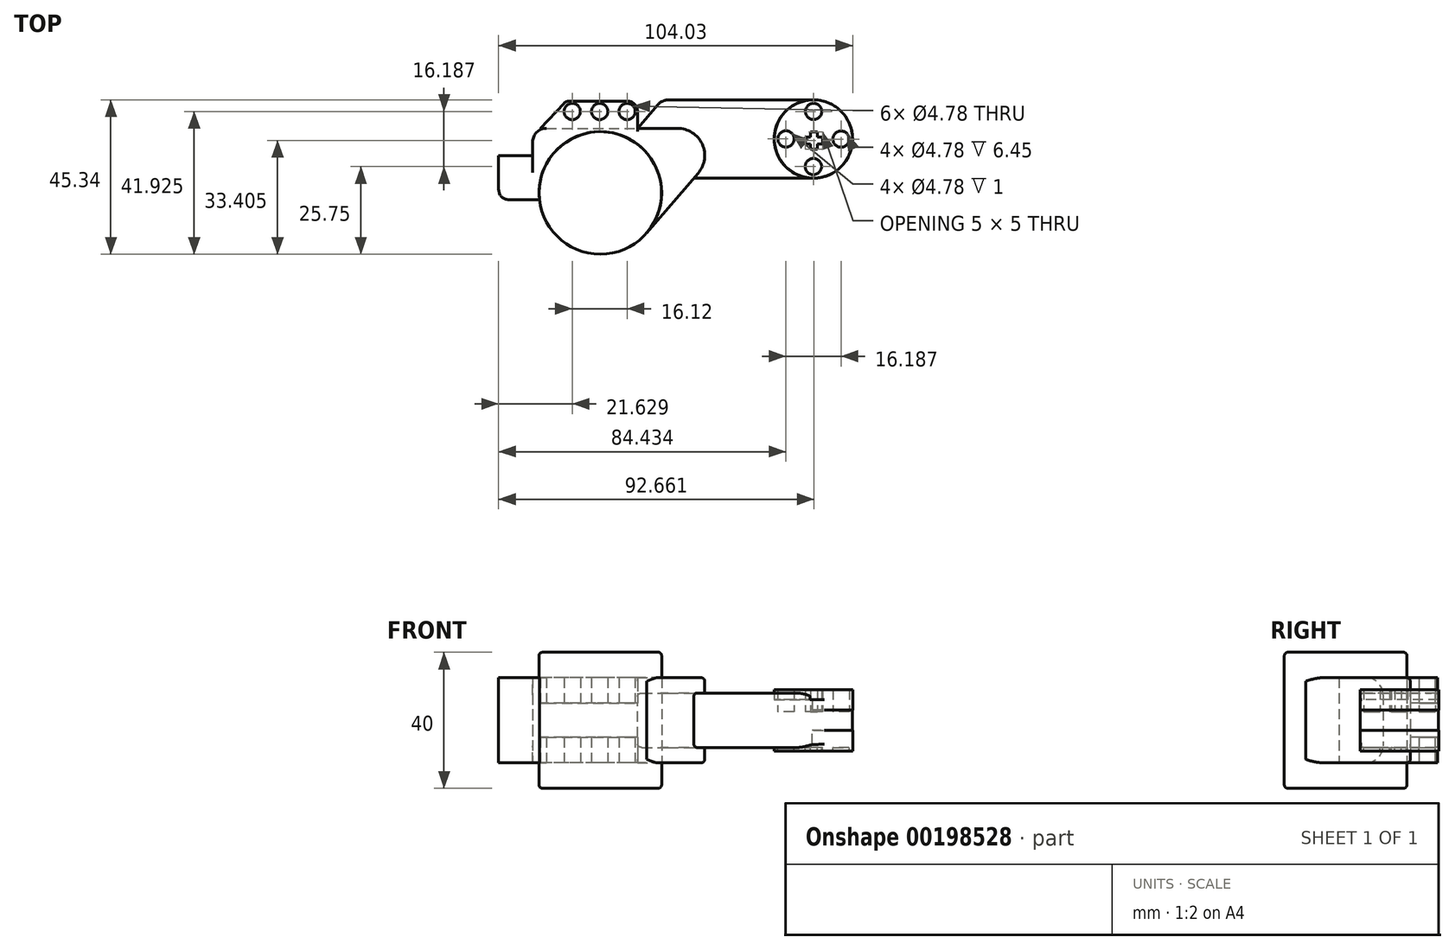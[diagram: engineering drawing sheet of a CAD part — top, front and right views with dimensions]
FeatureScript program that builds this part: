
annotation { "Feature Type Name" : "Feature", "Feature Type Description" : "" }
export const myFeature = defineFeature(function(context is Context, id is Id, definition is map)
    precondition{}
    {
        {
            var Q0;
            Q0=qCreatedBy(makeId("Top.planeOp"),FACE);
            var sketch = newSketch(context, id + "F0", { "sketchPlane" : qUnion([Q0])});
            skCircle(sketch, "E0", {"center": v(-41.3, 0) * mm, "radius": 18 * mm});
            skLineSegment(sketch, "E1", {"start": v(-57.19, 19) * mm, "end": v(-18.63, 19) * mm});
            skLineSegment(sketch, "E2", {"start": v(-12.57, 5.78) * mm, "end": v(-27.66, -11.74) * mm});
            skLineSegment(sketch, "E3", {"start": v(-61.19, 15) * mm, "end": v(-61.19, 11) * mm});
            skLineSegment(sketch, "E4", {"start": v(-61.19, 11) * mm, "end": v(-71.19, 11) * mm});
            skLineSegment(sketch, "E5", {"start": v(-71.19, 11) * mm, "end": v(-71.19, 1) * mm});
            skPoint(sketch, "E6.visualSharp", {"position": v(-1.19, 19) * mm});
            skLineSegment(sketch, "E7", {"start": v(-68.19, -2) * mm, "end": v(-59.19, -2) * mm});
            skArc(sketch, "E8.filletArc", {"start": v(-12.57, 5.78) * mm, "mid": v(-11.36, 14.33) * mm, "end": v(-18.63, 19) * mm});
            skPoint(sketch, "E9.visualSharp", {"position": v(-61.19, 19) * mm});
            skArc(sketch, "E9.filletArc", {"start": v(-57.19, 19) * mm, "mid": v(-60.02, 17.83) * mm, "end": v(-61.19, 15) * mm});
            skPoint(sketch, "E10.visualSharp", {"position": v(-71.19, -2) * mm});
            skArc(sketch, "E10.filletArc", {"start": v(-71.19, 1) * mm, "mid": v(-70.3, -1.12) * mm, "end": v(-68.19, -2) * mm});
            skLineSegment(sketch, "E11", {"start": v(-33.44, 27) * mm, "end": v(-50.5, 27) * mm});
            skLineSegment(sketch, "E12", {"start": v(-51.96, 26.37) * mm, "end": v(-60.1, 17.74) * mm});
            skLineSegment(sketch, "E13", {"start": v(-30.37, 23.92) * mm, "end": v(-30.37, 19) * mm});
            skPoint(sketch, "E14.visualSharp", {"position": v(-51.37, 27) * mm});
            skArc(sketch, "E14.filletArc", {"start": v(-50.5, 27) * mm, "mid": v(-51.3, 26.84) * mm, "end": v(-51.96, 26.37) * mm});
            skPoint(sketch, "E15.visualSharp", {"position": v(-30.37, 27) * mm});
            skArc(sketch, "E15.filletArc", {"start": v(-30.37, 23.92) * mm, "mid": v(-31.27, 26.1) * mm, "end": v(-33.44, 27) * mm});
            skLineSegment(sketch, "E16", {"start": v(-30.37, 19) * mm, "end": v(-58.91, 19) * mm, "construction": true});
            skLineSegment(sketch, "E17", {"start": v(-30.37, 19) * mm, "end": v(-23.19, 27.34) * mm});
            skLineSegment(sketch, "E18", {"start": v(-23.19, 27.34) * mm, "end": v(21.31, 27.34) * mm});
            skLineSegment(sketch, "E19", {"start": v(32.81, 15.84) * mm, "end": v(32.81, 15.84) * mm});
            skLineSegment(sketch, "E20", {"start": v(21.31, 4.34) * mm, "end": v(-13.81, 4.34) * mm});
            skPoint(sketch, "E21.visualSharp", {"position": v(32.81, 27.34) * mm});
            skArc(sketch, "E21.filletArc", {"start": v(32.81, 15.84) * mm, "mid": v(29.44, 23.97) * mm, "end": v(21.31, 27.34) * mm});
            skPoint(sketch, "E22.visualSharp", {"position": v(32.81, 4.34) * mm});
            skArc(sketch, "E22.filletArc", {"start": v(21.31, 4.34) * mm, "mid": v(29.44, 7.7) * mm, "end": v(32.81, 15.84) * mm});
            skLineSegment(sketch, "E23", {"start": v(-58.91, 19) * mm, "end": v(-30.37, 19) * mm});
            skCircle(sketch, "E24", {"center": v(-33.44, 23.92) * mm, "radius": 2.4 * mm});
            skCircle(sketch, "E25", {"center": v(-33.44, 23.92) * mm, "radius": 3.08 * mm, "construction": true});
            skCircle(sketch, "E26.1.0.0", {"center": v(-41.5, 23.92) * mm, "radius": 2.4 * mm});
            skCircle(sketch, "E26.2.0.0", {"center": v(-49.56, 23.92) * mm, "radius": 2.4 * mm});
            skLineSegment(sketch, "E26.direction1", {"start": v(-33.44, 23.92) * mm, "end": v(-41.5, 23.92) * mm, "construction": true});
            skSolve(sketch);
        }
        {
            var Q0;
            {var subQ0=sQuery(id+"F0.wireOp",EDGE,"E0");var subQ1=makeQuery(id+"F0.imprint","INTERSECT",VERTEX,{"derivedFrom":[subQ0,sQuery(id+"F0.wireOp",EDGE,"E2")]});Q0=makeQuery(id+"F0.imprint","IMPRINT",FACE,{"disambiguationData":[TD([[makeQuery(id+"F0.imprint","IMPRINT",EDGE,{"disambiguationData":[TD([[subQ1,1.0]])],"derivedFrom":subQ0}),1.0]])]});}
            var Q1;
            Q1=sQuery(id+"F0.wireOp",EDGE,"E0");
            extrude(context, id + "F1", {"entities" : qUnion([Q0]), "surfaceEntities" : qUnion([Q1]), "endBound" : BoundingType.SYMMETRIC, "depth" : 40 * mm});
        }
        {
            var Q0;
            {var subQ0=sQuery(id+"F0.wireOp",EDGE,"E3");Q0=makeQuery(id+"F0.imprint","IMPRINT",FACE,{"disambiguationData":[TD([[makeQuery(id+"F0.imprint","IMPRINT",EDGE,{"derivedFrom":subQ0}),1.0]])]});}
            var Q1;
            Q1=makeQuery(id+"F0.imprint","IMPRINT",FACE,{"disambiguationData":[TD([[makeQuery(id+"F0.imprint","IMPRINT",EDGE,{"derivedFrom":sQuery(id+"F0.wireOp",EDGE,"E11")}),1.0]])]});
            extrude(context, id + "F2", {"entities" : qUnion([Q0, Q1]), "endBound" : BoundingType.SYMMETRIC, "depth" : 25 * mm});
        }
        {
            var Q0;
            {var subQ0=sQuery(id+"F0.wireOp",EDGE,"E8.filletArc");Q0=makeQuery(id+"F0.imprint","IMPRINT",FACE,{"disambiguationData":[TD([[makeQuery(id+"F0.imprint","IMPRINT",EDGE,{"derivedFrom":subQ0}),-1.0]])]});}
            extrude(context, id + "F3", {"entities" : qUnion([Q0]), "operationType" : NewBodyOperationType.ADD, "endBound" : BoundingType.SYMMETRIC, "depth" : 16 * mm});
        }
        {
            var Q0;
            Q0=makeQuery(id+"F3.opExtrude","SWEPT_EDGE",EDGE,{"disambiguationData":[OSD([sQuery(id+"F0.wireOp",EDGE,"E17"),sQuery(id+"F0.wireOp",EDGE,"E18")])]});
            fillet(context, id + "F4", {"entities" : qUnion([Q0]), "radius" : 4 * mm, "tangentPropagation" : true, "allowEdgeOverflow" : false});
        }
        {
            var Q0;
            Q0=makeQuery(id+"F1.opExtrude","CAP_EDGE",EDGE,{"disambiguationData":[OSD([sQuery(id+"F0.wireOp",EDGE,"E0")])],"isStart":false});
            var Q1;
            Q1=makeQuery(id+"F1.opExtrude","CAP_EDGE",EDGE,{"disambiguationData":[OSD([sQuery(id+"F0.wireOp",EDGE,"E0")])],"isStart":true});
            fillet(context, id + "F5", {"entities" : qUnion([Q0, Q1]), "radius" : 1 * mm, "tangentPropagation" : true, "allowEdgeOverflow" : false});
        }
        {
            var Q0;
            Q0=makeQuery(id+"F2.opExtrude","CAP_EDGE",EDGE,{"disambiguationData":[OSD([sQuery(id+"F0.wireOp",EDGE,"E4")])],"isStart":false});
            var Q1;
            Q1=makeQuery(id+"F2.opExtrude","CAP_EDGE",EDGE,{"disambiguationData":[OSD([sQuery(id+"F0.wireOp",EDGE,"E4")])],"isStart":true});
            fillet(context, id + "F6", {"entities" : qUnion([Q0, Q1]), "radius" : 5 * mm, "tangentPropagation" : true, "allowEdgeOverflow" : false});
        }
        {
            var Q0;
            Q0=makeQuery(id+"F2.opExtrude","CAP_EDGE",EDGE,{"disambiguationData":[OSD([sQuery(id+"F0.wireOp",EDGE,"E1")])],"isStart":false});
            var Q1;
            Q1=makeQuery(id+"F2.opExtrude","CAP_EDGE",EDGE,{"disambiguationData":[OSD([sQuery(id+"F0.wireOp",EDGE,"E8.filletArc")])],"isStart":false});
            var Q2;
            Q2=makeQuery(id+"F2.opExtrude","CAP_EDGE",EDGE,{"disambiguationData":[OSD([sQuery(id+"F0.wireOp",EDGE,"E2")])],"isStart":false});
            var Q3;
            Q3=makeQuery(id+"F2.opExtrude","CAP_EDGE",EDGE,{"disambiguationData":[OSD([sQuery(id+"F0.wireOp",EDGE,"E1")])],"isStart":true});
            fillet(context, id + "F7", {"entities" : qUnion([Q0, Q1, Q2, Q3]), "radius" : 1 * mm, "tangentPropagation" : true, "allowEdgeOverflow" : false});
        }
        {
            var Q0;
            Q0=makeQuery(id+"F3.opExtrude","CAP_EDGE",EDGE,{"disambiguationData":[OSD([sQuery(id+"F0.wireOp",EDGE,"E18")])],"isStart":false});
            var Q1;
            Q1=makeQuery(id+"F3.opExtrude","CAP_EDGE",EDGE,{"disambiguationData":[OSD([sQuery(id+"F0.wireOp",EDGE,"E18")])],"isStart":true});
            fillet(context, id + "F8", {"entities" : qUnion([Q0, Q1]), "radius" : 1 * mm, "tangentPropagation" : true, "allowEdgeOverflow" : false});
        }
        {
            var Q0;
            Q0=makeQuery(id+"F0.imprint","IMPRINT",FACE,{"disambiguationData":[TD([[makeQuery(id+"F0.imprint","IMPRINT",EDGE,{"derivedFrom":sQuery(id+"F0.wireOp",EDGE,"E11")}),1.0]])]});
            extrude(context, id + "F9", {"entities" : qUnion([Q0]), "operationType" : NewBodyOperationType.REMOVE, "endBound" : BoundingType.SYMMETRIC, "oppositeDirection" : true, "depth" : 10 * mm});
        }
        {
            var Q0;
            Q0=makeQuery(id+"F0.imprint","IMPRINT",FACE,{"disambiguationData":[TD([[makeQuery(id+"F0.imprint","IMPRINT",EDGE,{"derivedFrom":sQuery(id+"F0.wireOp",EDGE,"E24")}),1.0]])]});
            var Q1;
            Q1=sQuery(id+"F0.wireOp",EDGE,"E24");
            extrude(context, id + "F10", {"entities" : qUnion([Q0]), "operationType" : NewBodyOperationType.REMOVE, "surfaceEntities" : qUnion([Q1]), "endBound" : BoundingType.SYMMETRIC, "oppositeDirection" : true, "depth" : 25 * mm});
        }
        {
            var Q0;
            Q0=qCreatedBy(makeId("Top.planeOp"),FACE);
            cPlane(context, id + "F11", {"entities" : qUnion([Q0]), "cplaneType" : CPlaneType.OFFSET, "offset" : 6 * mm, "width" : 150 * mm, "height" : 150 * mm});
        }
        {
            var Q0;
            Q0=qCreatedBy(id+"F11.planeOp",FACE);
            var sketch = newSketch(context, id + "F12", { "sketchPlane" : qUnion([Q0])});
            skCircle(sketch, "E27", {"center": v(21.34, 15.84) * mm, "radius": 11.55 * mm});
            skLineSegment(sketch, "E28", {"start": v(9.85, 17.04) * mm, "end": v(32.83, 17.04) * mm, "construction": true});
            skLineSegment(sketch, "E29", {"start": v(21.36, 27.4) * mm, "end": v(21.36, 4.3) * mm, "construction": true});
            skCircle(sketch, "E30", {"center": v(21.36, 23.94) * mm, "radius": 2.4 * mm});
            skCircle(sketch, "E31.1.0", {"center": v(13.24, 15.87) * mm, "radius": 2.4 * mm});
            skLineSegment(sketch, "E31.1.1", {"start": v(9.79, 15.87) * mm, "end": v(32.89, 15.87) * mm, "construction": true});
            skCircle(sketch, "E31.2.0", {"center": v(21.31, 7.75) * mm, "radius": 2.4 * mm});
            skLineSegment(sketch, "E31.2.1", {"start": v(21.31, 4.3) * mm, "end": v(21.31, 27.4) * mm, "construction": true});
            skCircle(sketch, "E31.3.0", {"center": v(29.43, 15.82) * mm, "radius": 2.4 * mm});
            skLineSegment(sketch, "E31.3.1", {"start": v(32.89, 15.82) * mm, "end": v(9.79, 15.82) * mm, "construction": true});
            skLineSegment(sketch, "E32", {"start": v(20.47, 17.9) * mm, "end": v(22.47, 17.9) * mm});
            skLineSegment(sketch, "E33", {"start": v(22.47, 17.9) * mm, "end": v(22.47, 16.4) * mm});
            skLineSegment(sketch, "E34", {"start": v(22.47, 16.4) * mm, "end": v(23.97, 16.4) * mm});
            skLineSegment(sketch, "E35", {"start": v(23.97, 16.4) * mm, "end": v(23.97, 14.4) * mm});
            skLineSegment(sketch, "E36", {"start": v(23.97, 14.4) * mm, "end": v(22.47, 14.4) * mm});
            skLineSegment(sketch, "E37", {"start": v(20.47, 14.4) * mm, "end": v(18.97, 14.4) * mm});
            skLineSegment(sketch, "E38", {"start": v(18.97, 14.4) * mm, "end": v(18.97, 16.4) * mm});
            skLineSegment(sketch, "E39", {"start": v(18.97, 16.4) * mm, "end": v(20.47, 16.4) * mm});
            skLineSegment(sketch, "E40", {"start": v(20.47, 16.4) * mm, "end": v(20.47, 17.9) * mm});
            skLineSegment(sketch, "E41", {"start": v(20.47, 14.4) * mm, "end": v(20.47, 12.9) * mm});
            skLineSegment(sketch, "E42", {"start": v(22.47, 14.4) * mm, "end": v(22.47, 12.9) * mm});
            skLineSegment(sketch, "E43", {"start": v(20.47, 12.9) * mm, "end": v(22.47, 12.9) * mm});
            skCircle(sketch, "E44.0", {"center": v(21.34, 15.84) * mm, "radius": 11.5 * mm});
            skSolve(sketch);
        }
        {
            var Q0;
            Q0=makeQuery(id+"F12.imprint","IMPRINT",FACE,{"disambiguationData":[TD([[makeQuery(id+"F12.imprint","IMPRINT",EDGE,{"derivedFrom":sQuery(id+"F12.wireOp",EDGE,"E27")}),1.0]])]});
            var Q1;
            Q1=sQuery(id+"F12.wireOp",EDGE,"E27");
            extrude(context, id + "F13", {"entities" : qUnion([Q0]), "operationType" : NewBodyOperationType.REMOVE, "surfaceEntities" : qUnion([Q1]), "depth" : 10 * mm});
        }
        {
            var Q0;
            Q0=makeQuery(id+"F12.imprint","IMPRINT",FACE,{"disambiguationData":[TD([[makeQuery(id+"F12.imprint","IMPRINT",EDGE,{"derivedFrom":sQuery(id+"F12.wireOp",EDGE,"E30")}),-1.0]])]});
            extrude(context, id + "F14", {"entities" : qUnion([Q0]), "endBound" : BoundingType.SYMMETRIC, "depth" : 6 * mm});
        }
        {
            var Q0;
            Q0=makeQuery(id+"F12.imprint","IMPRINT",FACE,{"disambiguationData":[TD([[makeQuery(id+"F12.imprint","IMPRINT",EDGE,{"derivedFrom":sQuery(id+"F12.wireOp",EDGE,"E32")}),-1.0]])]});
            var Q1;
            Q1=makeQuery(id+"F12.imprint","IMPRINT",FACE,{"disambiguationData":[TD([[makeQuery(id+"F12.imprint","IMPRINT",EDGE,{"derivedFrom":sQuery(id+"F12.wireOp",EDGE,"E30")}),1.0]])]});
            var Q2;
            Q2=makeQuery(id+"F12.imprint","IMPRINT",FACE,{"disambiguationData":[TD([[makeQuery(id+"F12.imprint","IMPRINT",EDGE,{"derivedFrom":sQuery(id+"F12.wireOp",EDGE,"E31.1.0")}),1.0]])]});
            var Q3;
            Q3=makeQuery(id+"F12.imprint","IMPRINT",FACE,{"disambiguationData":[TD([[makeQuery(id+"F12.imprint","IMPRINT",EDGE,{"derivedFrom":sQuery(id+"F12.wireOp",EDGE,"E31.3.0")}),1.0]])]});
            var Q4;
            Q4=makeQuery(id+"F12.imprint","IMPRINT",FACE,{"disambiguationData":[TD([[makeQuery(id+"F12.imprint","IMPRINT",EDGE,{"derivedFrom":sQuery(id+"F12.wireOp",EDGE,"E31.2.0")}),1.0]])]});
            extrude(context, id + "F15", {"entities" : qUnion([Q0, Q1, Q2, Q3, Q4]), "operationType" : NewBodyOperationType.REMOVE, "endBound" : BoundingType.SYMMETRIC, "depth" : 6.9 * mm});
        }
        {
            var Q0;
            Q0=makeQuery(id+"F14.opExtrude","SWEPT_BODY",BODY,{"disambiguationData":[OSD([sQuery(id+"F12.wireOp",EDGE,"E30"),sQuery(id+"F12.wireOp",EDGE,"E31.1.0"),sQuery(id+"F12.wireOp",EDGE,"E31.2.0"),sQuery(id+"F12.wireOp",EDGE,"E31.3.0"),sQuery(id+"F12.wireOp",EDGE,"E32"),sQuery(id+"F12.wireOp",EDGE,"E33"),sQuery(id+"F12.wireOp",EDGE,"E34"),sQuery(id+"F12.wireOp",EDGE,"E35"),sQuery(id+"F12.wireOp",EDGE,"E36"),sQuery(id+"F12.wireOp",EDGE,"E37"),sQuery(id+"F12.wireOp",EDGE,"E38"),sQuery(id+"F12.wireOp",EDGE,"E39"),sQuery(id+"F12.wireOp",EDGE,"E40"),sQuery(id+"F12.wireOp",EDGE,"E41"),sQuery(id+"F12.wireOp",EDGE,"E42"),sQuery(id+"F12.wireOp",EDGE,"E43"),sQuery(id+"F12.wireOp",EDGE,"E44.0")])]});
            var Q1;
            Q1=qCreatedBy(makeId("Top.planeOp"),FACE);
            mirror(context, id + "F16", {"operationType" : NewBodyOperationType.ADD, "entities" : qUnion([Q0]), "mirrorPlane" : qUnion([Q1])});
        }
    });
